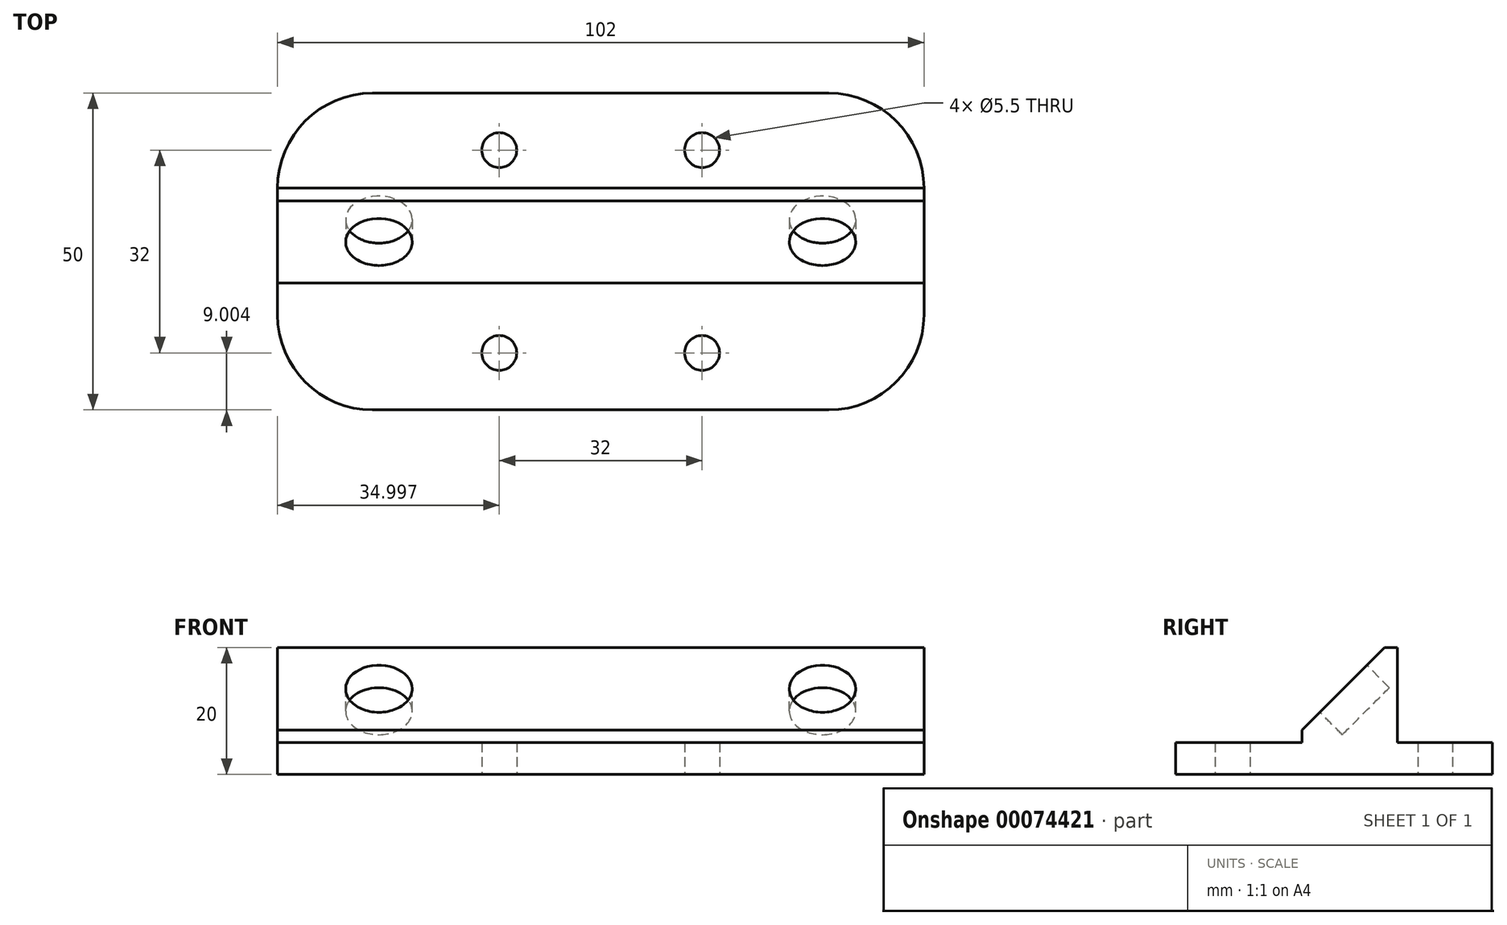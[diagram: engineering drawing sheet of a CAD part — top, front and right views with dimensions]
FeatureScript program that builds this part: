
annotation { "Feature Type Name" : "Feature", "Feature Type Description" : "" }
export const myFeature = defineFeature(function(context is Context, id is Id, definition is map)
    precondition{}
    {
        {
            var Q0;
            Q0=qCreatedBy(makeId("Top.planeOp"),FACE);
            var sketch = newSketch(context, id + "F0", { "sketchPlane" : qUnion([Q0])});
            skLineSegment(sketch, "E0.bottom", {"start": v(19.29, 1.32) * mm, "end": v(51.29, 1.32) * mm, "construction": true});
            skLineSegment(sketch, "E0.top", {"start": v(19.29, -30.68) * mm, "end": v(51.29, -30.68) * mm, "construction": true});
            skLineSegment(sketch, "E0.left", {"start": v(19.29, 1.32) * mm, "end": v(19.29, -30.68) * mm, "construction": true});
            skLineSegment(sketch, "E0.right", {"start": v(51.29, 1.32) * mm, "end": v(51.29, -30.68) * mm, "construction": true});
            skCircle(sketch, "E1", {"center": v(19.29, 1.32) * mm, "radius": 2.75 * mm});
            skCircle(sketch, "E2", {"center": v(51.29, 1.32) * mm, "radius": 2.75 * mm});
            skCircle(sketch, "E3", {"center": v(51.29, -30.68) * mm, "radius": 2.75 * mm});
            skCircle(sketch, "E4", {"center": v(19.29, -30.68) * mm, "radius": 2.75 * mm});
            skLineSegment(sketch, "E5.bottom", {"start": v(-15.71, 10.32) * mm, "end": v(86.29, 10.32) * mm});
            skLineSegment(sketch, "E5.top", {"start": v(-15.71, -39.68) * mm, "end": v(86.29, -39.68) * mm});
            skLineSegment(sketch, "E5.left", {"start": v(-15.71, 10.32) * mm, "end": v(-15.71, -39.68) * mm});
            skLineSegment(sketch, "E5.right", {"start": v(86.29, 10.32) * mm, "end": v(86.29, -39.68) * mm});
            skSolve(sketch);
        }
        {
            var Q0;
            Q0=makeQuery(id+"F0.imprint","IMPRINT",FACE,{"disambiguationData":[TD([[makeQuery(id+"F0.imprint","IMPRINT",EDGE,{"derivedFrom":sQuery(id+"F0.wireOp",EDGE,"E1")}),-1.0]])]});
            extrude(context, id + "F1", {"entities" : qUnion([Q0]), "depth" : 5 * mm});
        }
        {
            var Q0;
            Q0=makeQuery(id+"F1.opExtrude","CAP_FACE",FACE,{"disambiguationData":[OSD([sQuery(id+"F0.wireOp",EDGE,"E1"),sQuery(id+"F0.wireOp",EDGE,"E2"),sQuery(id+"F0.wireOp",EDGE,"E3"),sQuery(id+"F0.wireOp",EDGE,"E4"),sQuery(id+"F0.wireOp",EDGE,"E5.bottom"),sQuery(id+"F0.wireOp",EDGE,"E5.top"),sQuery(id+"F0.wireOp",EDGE,"E5.left"),sQuery(id+"F0.wireOp",EDGE,"E5.right")])],"isStart":false});
            var sketch = newSketch(context, id + "F2", { "sketchPlane" : qUnion([Q0])});
            skLineSegment(sketch, "E6", {"start": v(-15.71, -4.68) * mm, "end": v(86.29, -4.68) * mm});
            skLineSegment(sketch, "E7", {"start": v(86.29, -4.68) * mm, "end": v(86.29, -19.68) * mm});
            skLineSegment(sketch, "E8", {"start": v(86.29, -19.68) * mm, "end": v(-15.71, -19.68) * mm});
            skLineSegment(sketch, "E9", {"start": v(-15.71, -19.68) * mm, "end": v(-15.71, -4.68) * mm});
            skSolve(sketch);
        }
        {
            var Q0;
            Q0=makeQuery(id+"F2.imprint","IMPRINT",FACE,{"disambiguationData":[TD([[makeQuery(id+"F2.imprint","IMPRINT",EDGE,{"derivedFrom":sQuery(id+"F2.wireOp",EDGE,"E6")}),-1.0]])]});
            extrude(context, id + "F3", {"entities" : qUnion([Q0]), "operationType" : NewBodyOperationType.ADD, "depth" : 15 * mm});
        }
        {
            var Q0;
            Q0=makeQuery(id+"F3.opExtrude","CAP_EDGE",EDGE,{"disambiguationData":[OSD([sQuery(id+"F2.wireOp",EDGE,"E8")])],"isStart":false});
            chamfer(context, id + "F4", {"entities" : qUnion([Q0]), "width" : 13 * mm, "tangentPropagation" : true});
        }
        {
            var Q0;
            Q0=makeQuery(id+"F1.opExtrude","SWEPT_EDGE",EDGE,{"disambiguationData":[OSD([sQuery(id+"F0.wireOp",EDGE,"E5.bottom"),sQuery(id+"F0.wireOp",EDGE,"E5.right")])]});
            var Q1;
            Q1=makeQuery(id+"F1.opExtrude","SWEPT_EDGE",EDGE,{"disambiguationData":[OSD([sQuery(id+"F0.wireOp",EDGE,"E5.bottom"),sQuery(id+"F0.wireOp",EDGE,"E5.left")])]});
            var Q2;
            Q2=makeQuery(id+"F1.opExtrude","SWEPT_EDGE",EDGE,{"disambiguationData":[OSD([sQuery(id+"F0.wireOp",EDGE,"E5.top"),sQuery(id+"F0.wireOp",EDGE,"E5.right")])]});
            var Q3;
            Q3=makeQuery(id+"F1.opExtrude","SWEPT_EDGE",EDGE,{"disambiguationData":[OSD([sQuery(id+"F0.wireOp",EDGE,"E5.top"),sQuery(id+"F0.wireOp",EDGE,"E5.left")])]});
            fillet(context, id + "F5", {"entities" : qUnion([Q0, Q1, Q2, Q3]), "radius" : 15 * mm, "tangentPropagation" : true, "allowEdgeOverflow" : false});
        }
        {
            var Q0;
            Q0=makeQuery(id+"F4.opChamfer","BLEND_FACE",FACE,{"disambiguationData":[OSD([sQuery(id+"F2.wireOp",EDGE,"E8")])]});
            var sketch = newSketch(context, id + "F6", { "sketchPlane" : qUnion([Q0])});
            skLineSegment(sketch, "E10", {"start": v(86.29, 0.23) * mm, "end": v(-15.71, 0.23) * mm, "construction": true});
            skLineSegment(sketch, "E11", {"start": v(35.29, 0.23) * mm, "end": v(70.29, 0.23) * mm, "construction": true});
            skLineSegment(sketch, "E12", {"start": v(35.29, 0.23) * mm, "end": v(0.29, 0.23) * mm, "construction": true});
            skCircle(sketch, "E13", {"center": v(70.29, 0.23) * mm, "radius": 5.25 * mm});
            skCircle(sketch, "E14", {"center": v(0.29, 0.23) * mm, "radius": 5.25 * mm});
            skSolve(sketch);
        }
        {
            var Q0;
            Q0=makeQuery(id+"F6.imprint","IMPRINT",FACE,{"disambiguationData":[TD([[makeQuery(id+"F6.imprint","IMPRINT",EDGE,{"derivedFrom":sQuery(id+"F6.wireOp",EDGE,"E14")}),1.0]])]});
            var Q1;
            Q1=makeQuery(id+"F6.imprint","IMPRINT",FACE,{"disambiguationData":[TD([[makeQuery(id+"F6.imprint","IMPRINT",EDGE,{"derivedFrom":sQuery(id+"F6.wireOp",EDGE,"E13")}),1.0]])]});
            extrude(context, id + "F7", {"entities" : qUnion([Q0, Q1]), "operationType" : NewBodyOperationType.REMOVE, "oppositeDirection" : true, "depth" : 5 * mm});
        }
    });
